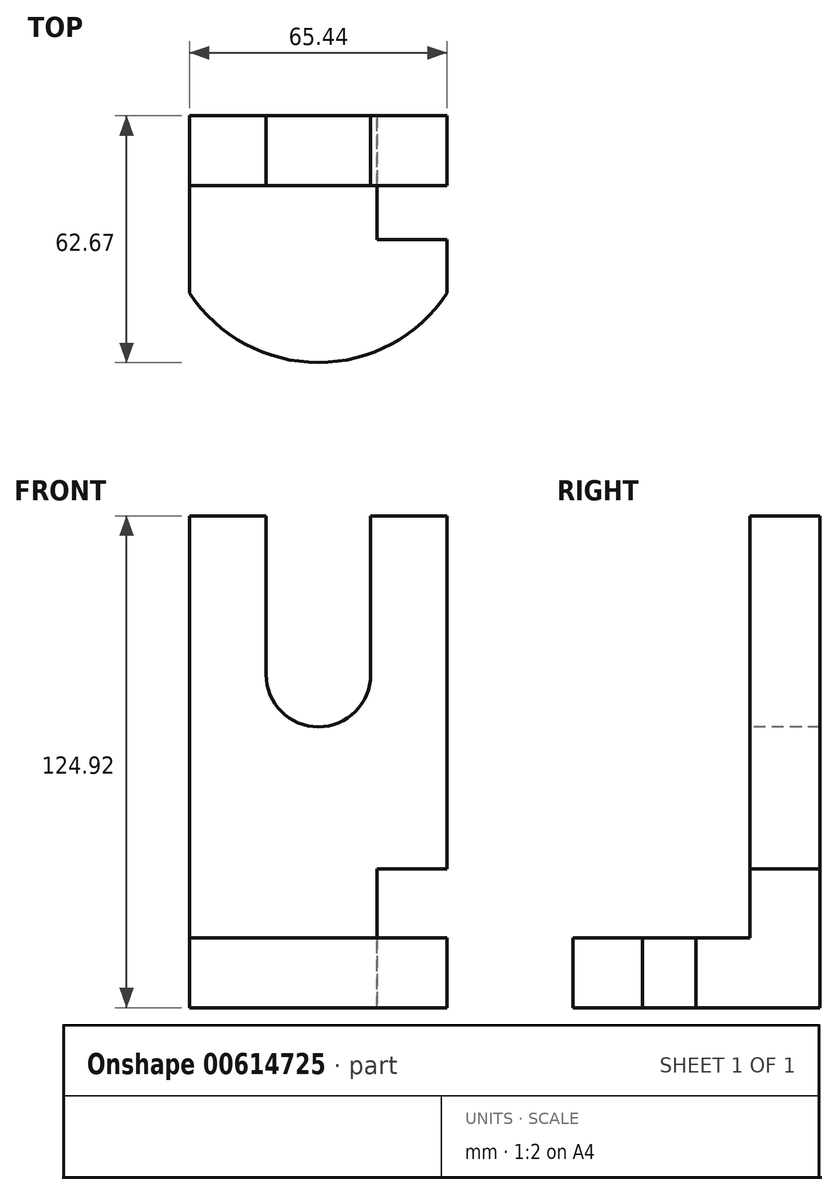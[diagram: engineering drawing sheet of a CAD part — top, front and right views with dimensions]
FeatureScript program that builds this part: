
annotation { "Feature Type Name" : "Feature", "Feature Type Description" : "" }
export const myFeature = defineFeature(function(context is Context, id is Id, definition is map)
    precondition{}
    {
        {
            var Q0;
            Q0=qCreatedBy(makeId("Front.planeOp"),FACE);
            var sketch = newSketch(context, id + "F0", { "sketchPlane" : qUnion([Q0])});
            skLineSegment(sketch, "E0.bottom", {"start": v(-32.72, -53.57) * mm, "end": v(32.72, -53.57) * mm});
            skLineSegment(sketch, "E0.top", {"start": v(-32.72, 53.57) * mm, "end": v(32.72, 53.57) * mm});
            skLineSegment(sketch, "E0.left", {"start": v(-32.72, -53.57) * mm, "end": v(-32.72, 53.57) * mm});
            skLineSegment(sketch, "E0.right", {"start": v(32.72, -53.57) * mm, "end": v(32.72, 53.57) * mm});
            skPoint(sketch, "E0.middle", {"position": v(0, 0) * mm});
            skSolve(sketch);
        }
        {
            var Q0;
            Q0 = qSketchRegion(id + "F0", true);
            extrude(context, id + "F1", {"entities" : qUnion([Q0]), "depth" : 17.78 * mm, "offsetDistance" : 25.4 * mm});
        }
        {
            var Q0;
            Q0=makeQuery(id+"F1.opExtrude","SWEPT_FACE",FACE,{"disambiguationData":[OSD([sQuery(id+"F0.wireOp",EDGE,"E0.bottom")])]});
            var sketch = newSketch(context, id + "F2", { "sketchPlane" : qUnion([Q0])});
            skLineSegment(sketch, "E1", {"start": v(-32.72, 0) * mm, "end": v(-32.72, 45.07) * mm});
            skLineSegment(sketch, "E2", {"start": v(-32.72, 45.07) * mm, "end": v(32.72, 45.07) * mm});
            skLineSegment(sketch, "E3", {"start": v(32.72, 45.07) * mm, "end": v(32.72, 0) * mm});
            skLineSegment(sketch, "E4", {"start": v(32.72, 0) * mm, "end": v(-32.72, 0) * mm});
            skArc(sketch, "E5", {"start": v(32.72, 45.07) * mm, "mid": v(0, 62.67) * mm, "end": v(-32.72, 45.07) * mm});
            skSolve(sketch);
        }
        {
            var Q0;
            Q0 = qSketchRegion(id + "F2", true);
            extrude(context, id + "F3", {"entities" : qUnion([Q0]), "operationType" : NewBodyOperationType.ADD, "depth" : 17.78 * mm, "offsetDistance" : 25.4 * mm});
        }
        {
            var Q0;
            Q0=makeQuery(id+"F3.boolean.opBoolean","MERGE",FACE,{"derivedFrom":[makeQuery(id+"F1.opExtrude","SWEPT_FACE",FACE,{"disambiguationData":[OSD([sQuery(id+"F0.wireOp",EDGE,"E0.right")])]}),makeQuery(id+"F3.opExtrude","SWEPT_FACE",FACE,{"disambiguationData":[OSD([sQuery(id+"F2.wireOp",EDGE,"E3")])]})]});
            var sketch = newSketch(context, id + "F4", { "sketchPlane" : qUnion([Q0])});
            skLineSegment(sketch, "E6", {"start": v(0, -36.14) * mm, "end": v(-17.78, -36.14) * mm});
            skLineSegment(sketch, "E7", {"start": v(-17.78, -36.14) * mm, "end": v(-17.78, -53.57) * mm});
            skLineSegment(sketch, "E8", {"start": v(-17.78, -53.57) * mm, "end": v(-31.43, -53.57) * mm});
            skLineSegment(sketch, "E9", {"start": v(-31.43, -53.57) * mm, "end": v(-31.43, -71.35) * mm});
            skLineSegment(sketch, "E10", {"start": v(-31.43, -71.35) * mm, "end": v(0, -71.35) * mm});
            skLineSegment(sketch, "E11", {"start": v(0, -71.35) * mm, "end": v(0, -36.14) * mm});
            skSolve(sketch);
        }
        {
            var Q0;
            Q0 = qSketchRegion(id + "F4", true);
            extrude(context, id + "F5", {"entities" : qUnion([Q0]), "operationType" : NewBodyOperationType.REMOVE, "oppositeDirection" : true, "depth" : 17.78 * mm, "offsetDistance" : 25.4 * mm});
        }
        {
            var Q0;
            Q0=makeQuery(id+"F1.opExtrude","CAP_FACE",FACE,{"disambiguationData":[OSD([sQuery(id+"F0.wireOp",EDGE,"E0.bottom"),sQuery(id+"F0.wireOp",EDGE,"E0.top"),sQuery(id+"F0.wireOp",EDGE,"E0.left"),sQuery(id+"F0.wireOp",EDGE,"E0.right")])],"isStart":false});
            var sketch = newSketch(context, id + "F6", { "sketchPlane" : qUnion([Q0])});
            skLineSegment(sketch, "E12.top", {"start": v(13.27, 93.87) * mm, "end": v(-13.27, 93.87) * mm});
            skLineSegment(sketch, "E12.left", {"start": v(13.27, 13.28) * mm, "end": v(13.27, 93.87) * mm});
            skLineSegment(sketch, "E12.right", {"start": v(-13.27, 13.28) * mm, "end": v(-13.27, 93.87) * mm});
            skPoint(sketch, "E12.middle", {"position": v(0, 53.57) * mm});
            skArc(sketch, "E13", {"start": v(-13.27, 13.28) * mm, "mid": v(0, 0) * mm, "end": v(13.27, 13.28) * mm});
            skSolve(sketch);
        }
        {
            var Q0;
            Q0 = qSketchRegion(id + "F6", true);
            extrude(context, id + "F7", {"entities" : qUnion([Q0]), "operationType" : NewBodyOperationType.REMOVE, "oppositeDirection" : true, "depth" : 25.4 * mm, "offsetDistance" : 25.4 * mm});
        }
    });
